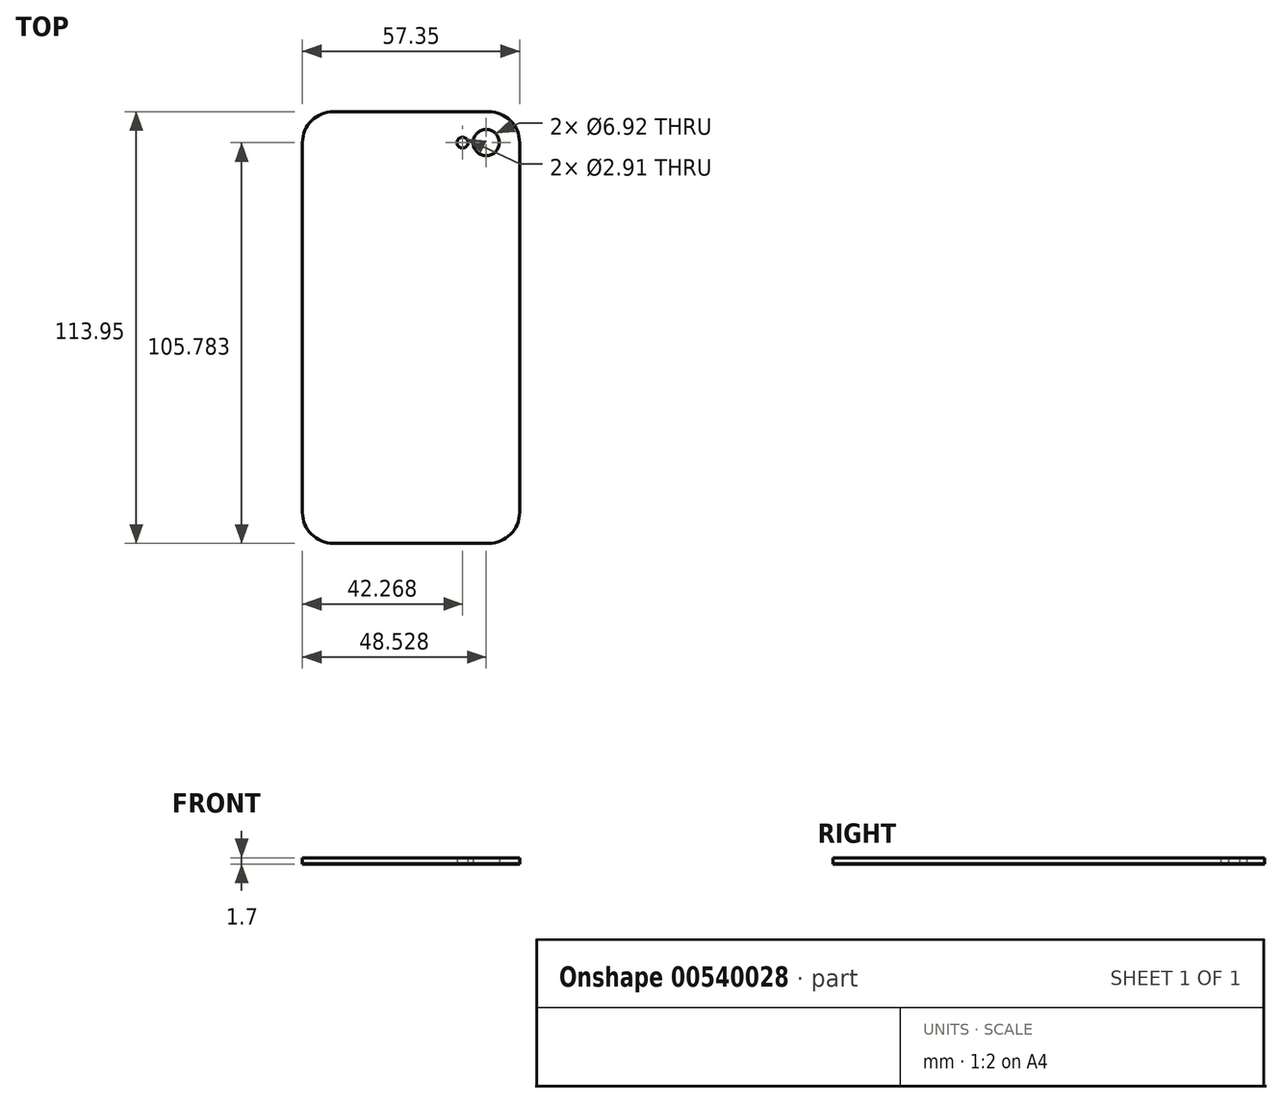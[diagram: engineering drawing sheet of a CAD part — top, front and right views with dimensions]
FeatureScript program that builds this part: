
annotation { "Feature Type Name" : "Feature", "Feature Type Description" : "" }
export const myFeature = defineFeature(function(context is Context, id is Id, definition is map)
    precondition{}
    {
        {
            var Q0;
            Q0=qCreatedBy(makeId("Top.planeOp"),FACE);
            var sketch = newSketch(context, id + "F0", { "sketchPlane" : qUnion([Q0])});
            skLineSegment(sketch, "E0.bottom", {"start": v(-20.18, 61.85) * mm, "end": v(20.83, 61.85) * mm});
            skLineSegment(sketch, "E0.top", {"start": v(-20.18, -52.1) * mm, "end": v(20.83, -52.1) * mm});
            skLineSegment(sketch, "E0.left", {"start": v(-28.35, 53.68) * mm, "end": v(-28.35, -43.93) * mm});
            skLineSegment(sketch, "E0.right", {"start": v(29, 53.68) * mm, "end": v(29, -43.93) * mm});
            skPoint(sketch, "E1.visualSharp", {"position": v(-28.35, 61.85) * mm});
            skArc(sketch, "E1.filletArc", {"start": v(-20.18, 61.85) * mm, "mid": v(-25.96, 59.46) * mm, "end": v(-28.35, 53.68) * mm});
            skPoint(sketch, "E2.visualSharp", {"position": v(29, 61.85) * mm});
            skArc(sketch, "E2.filletArc", {"start": v(29, 53.68) * mm, "mid": v(26.6, 59.46) * mm, "end": v(20.83, 61.85) * mm});
            skPoint(sketch, "E3.visualSharp", {"position": v(-28.35, -52.1) * mm});
            skArc(sketch, "E3.filletArc", {"start": v(-28.35, -43.93) * mm, "mid": v(-25.96, -49.7) * mm, "end": v(-20.18, -52.1) * mm});
            skPoint(sketch, "E4.visualSharp", {"position": v(29, -52.1) * mm});
            skArc(sketch, "E4.filletArc", {"start": v(20.83, -52.1) * mm, "mid": v(26.6, -49.7) * mm, "end": v(29, -43.93) * mm});
            skCircle(sketch, "E5.MirrorC", {"center": v(20.18, 53.68) * mm, "radius": 3.46 * mm});
            skCircle(sketch, "E6.MirrorC", {"center": v(13.92, 53.68) * mm, "radius": 1.46 * mm});
            skSolve(sketch);
        }
        {
            var Q0;
            Q0=makeQuery(id+"F0.imprint","IMPRINT",FACE,{"disambiguationData":[TD([[makeQuery(id+"F0.imprint","IMPRINT",EDGE,{"derivedFrom":sQuery(id+"F0.wireOp",EDGE,"E0.bottom")}),-1.0]])]});
            extrude(context, id + "F1", {"entities" : qUnion([Q0]), "depth" : 1.6 * mm, "offsetDistance" : 25 * mm});
        }
        {
            var Q0;
            Q0=makeQuery(id+"F0.imprint","IMPRINT",FACE,{"disambiguationData":[TD([[makeQuery(id+"F0.imprint","IMPRINT",EDGE,{"derivedFrom":sQuery(id+"F0.wireOp",EDGE,"E5.MirrorC")}),-1.0]])]});
            extrude(context, id + "F2", {"entities" : qUnion([Q0]), "operationType" : NewBodyOperationType.ADD, "oppositeDirection" : true, "depth" : .1 * mm, "offsetDistance" : 25 * mm});
        }
        {
            var Q0;
            Q0=makeQuery(id+"F0.imprint","IMPRINT",FACE,{"disambiguationData":[TD([[makeQuery(id+"F0.imprint","IMPRINT",EDGE,{"derivedFrom":sQuery(id+"F0.wireOp",EDGE,"E6.MirrorC")}),-1.0]])]});
            extrude(context, id + "F3", {"entities" : qUnion([Q0]), "oppositeDirection" : true, "depth" : .1 * mm, "offsetDistance" : 25 * mm});
        }
    });
